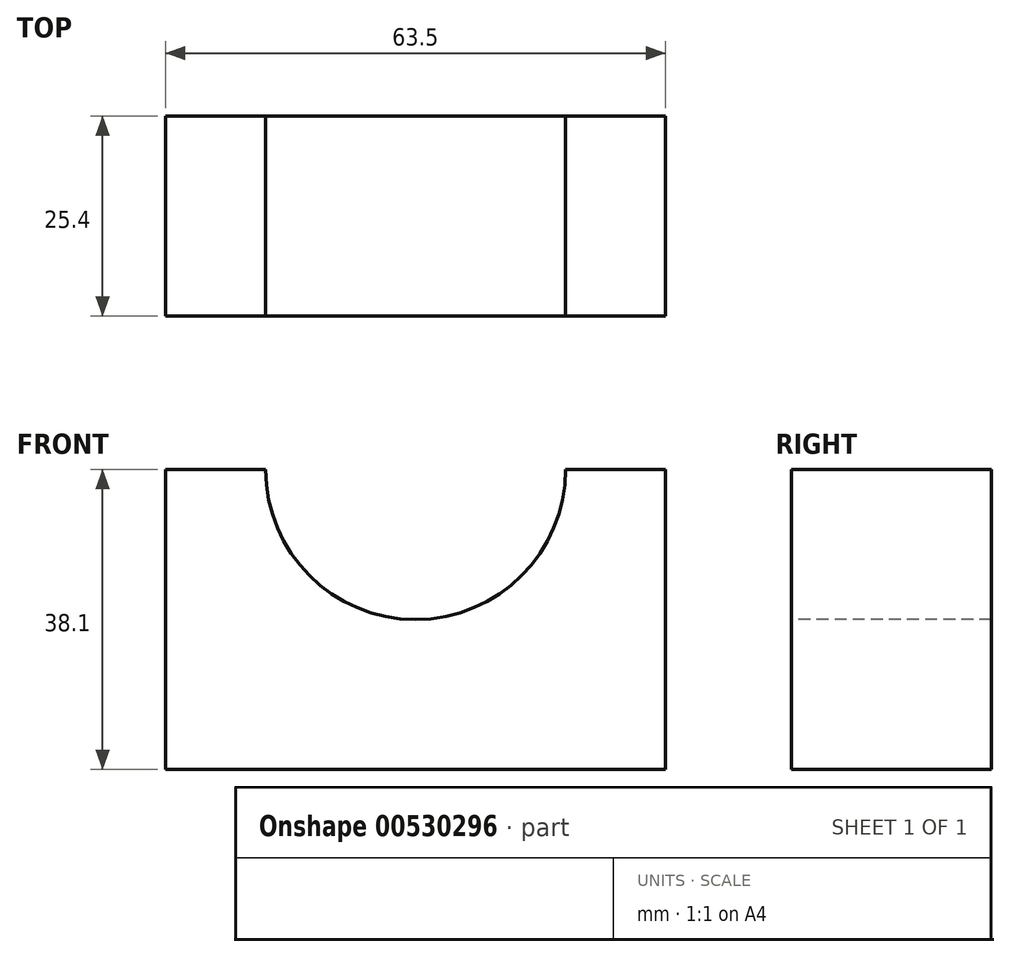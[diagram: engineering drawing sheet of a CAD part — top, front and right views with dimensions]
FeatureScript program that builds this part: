
annotation { "Feature Type Name" : "Feature", "Feature Type Description" : "" }
export const myFeature = defineFeature(function(context is Context, id is Id, definition is map)
    precondition{}
    {
        {
            var Q0;
            Q0=qCreatedBy(makeId("Front.planeOp"),FACE);
            var sketch = newSketch(context, id + "F0", { "sketchPlane" : qUnion([Q0])});
            skLineSegment(sketch, "E0", {"start": v(-40.04, 38.1) * mm, "end": v(-40.04, 0) * mm});
            skLineSegment(sketch, "E1", {"start": v(-40.04, 0) * mm, "end": v(23.46, 0) * mm});
            skLineSegment(sketch, "E2", {"start": v(23.46, 0) * mm, "end": v(23.46, 38.1) * mm});
            skLineSegment(sketch, "E3", {"start": v(23.46, 38.1) * mm, "end": v(-40.04, 38.1) * mm});
            skSolve(sketch);
        }
        {
            var Q0;
            Q0=makeQuery(id+"F0.imprint","IMPRINT",FACE,{"disambiguationData":[TD([[makeQuery(id+"F0.imprint","IMPRINT",EDGE,{"derivedFrom":sQuery(id+"F0.wireOp",EDGE,"E0")}),1.0]])]});
            extrude(context, id + "F1", {"entities" : qUnion([Q0]), "depth" : 25.4 * mm, "offsetDistance" : 25.4 * mm});
        }
        {
            var Q0;
            Q0=makeQuery(id+"F1.opExtrude","CAP_FACE",FACE,{"disambiguationData":[OSD([sQuery(id+"F0.wireOp",EDGE,"E0"),sQuery(id+"F0.wireOp",EDGE,"E1"),sQuery(id+"F0.wireOp",EDGE,"E2"),sQuery(id+"F0.wireOp",EDGE,"E3")])],"isStart":false});
            var sketch = newSketch(context, id + "F2", { "sketchPlane" : qUnion([Q0])});
            skArc(sketch, "E4", {"start": v(-27.34, 38.1) * mm, "mid": v(-8.29, 19.05) * mm, "end": v(10.76, 38.1) * mm});
            skSolve(sketch);
        }
        {
            var Q0;
            Q0 = qSketchRegion(id + "F2", true);
            var Q1;
            {var subQ0=sQuery(id+"F2.wireOp",EDGE,"E4");Q1=makeQuery(id+"F2.imprint","IMPRINT",FACE,{"disambiguationData":[TD([[makeQuery(id+"F2.imprint","IMPRINT",EDGE,{"derivedFrom":subQ0}),1.0]])]});}
            extrude(context, id + "F3", {"entities" : qUnion([Q0, Q1]), "operationType" : NewBodyOperationType.REMOVE, "endBound" : BoundingType.THROUGH_ALL, "oppositeDirection" : true, "depth" : 25.4 * mm, "offsetDistance" : 25.4 * mm});
        }
    });
